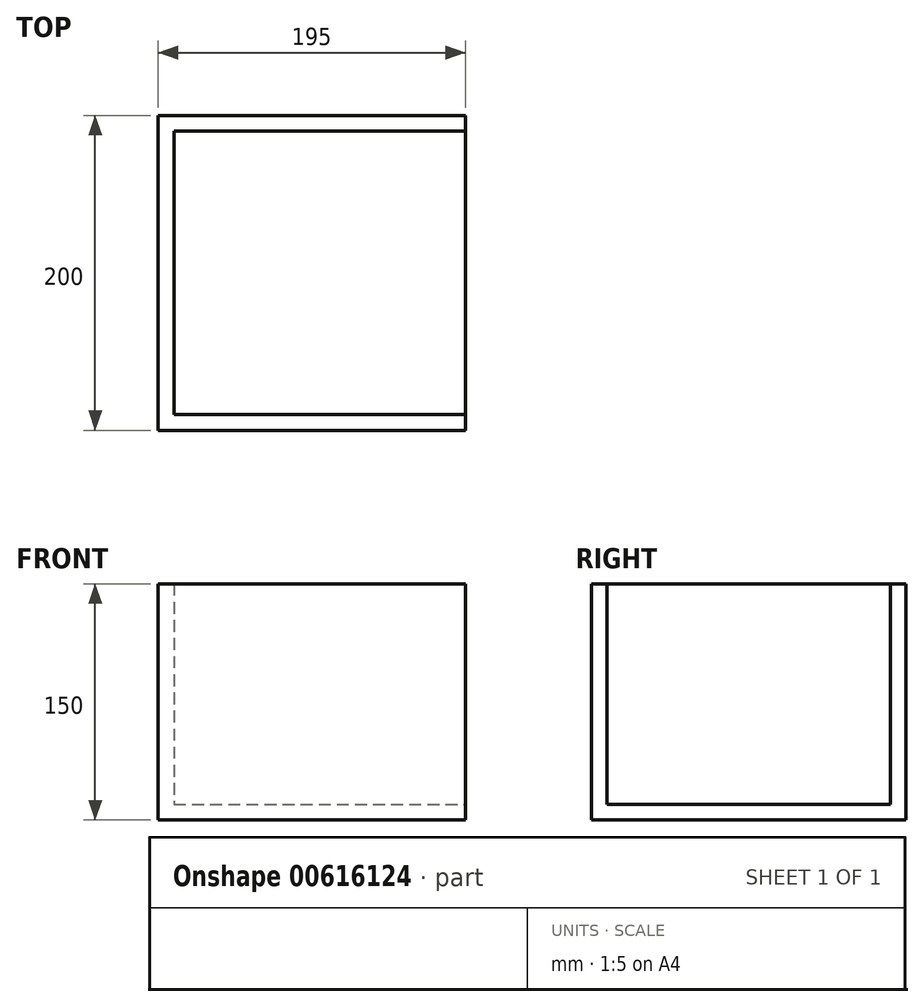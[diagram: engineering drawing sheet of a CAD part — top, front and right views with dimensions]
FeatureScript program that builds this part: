
annotation { "Feature Type Name" : "Feature", "Feature Type Description" : "" }
export const myFeature = defineFeature(function(context is Context, id is Id, definition is map)
    precondition{}
    {
        {
            var Q0;
            Q0=qCreatedBy(makeId("Top.planeOp"),FACE);
            var sketch = newSketch(context, id + "F0", { "sketchPlane" : qUnion([Q0])});
            skLineSegment(sketch, "E0.bottom", {"start": v(0, 0) * mm, "end": v(195, 0) * mm});
            skLineSegment(sketch, "E0.top", {"start": v(0, 200) * mm, "end": v(195, 200) * mm});
            skLineSegment(sketch, "E0.left", {"start": v(0, 0) * mm, "end": v(0, 200) * mm});
            skLineSegment(sketch, "E0.right", {"start": v(195, 0) * mm, "end": v(195, 200) * mm});
            skSolve(sketch);
        }
        {
            var Q0;
            Q0 = qSketchRegion(id + "F0", true);
            extrude(context, id + "F1", {"entities" : qUnion([Q0]), "depth" : 150 * mm, "offsetDistance" : 25 * mm});
        }
        {
            var Q0;
            Q0=makeQuery(id+"F1.opExtrude","CAP_FACE",FACE,{"disambiguationData":[OSD([sQuery(id+"F0.wireOp",EDGE,"E0.bottom"),sQuery(id+"F0.wireOp",EDGE,"E0.top"),sQuery(id+"F0.wireOp",EDGE,"E0.left"),sQuery(id+"F0.wireOp",EDGE,"E0.right")])],"isStart":false});
            var Q1;
            Q1=makeQuery(id+"F1.opExtrude","SWEPT_FACE",FACE,{"disambiguationData":[OSD([sQuery(id+"F0.wireOp",EDGE,"E0.right")])]});
            shell(context, id + "F2", {"entities" : qUnion([Q0, Q1]), "thickness" : 10 * mm});
        }
    });
